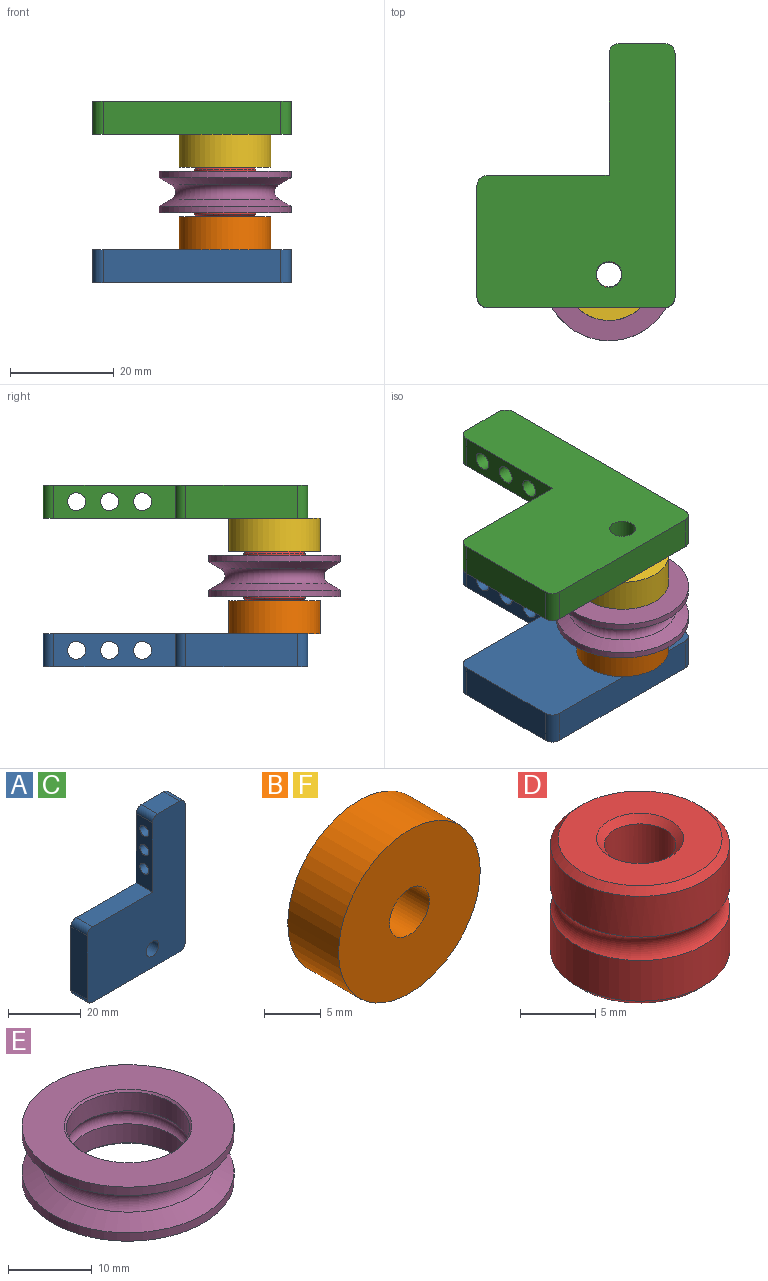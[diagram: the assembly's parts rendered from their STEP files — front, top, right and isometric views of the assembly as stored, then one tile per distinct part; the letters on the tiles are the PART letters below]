
ASSEMBLY  parts=6 mates=5
PART A: 17 faces, bbox 38.1x6.4x50.8 mm
  f0: plane 23.4x6.35mm, normal (0,0,1), area 148.6mm2, adj f6,f7,f8,f9
  f1: plane 21.4x6.35mm, normal (-1,0,0), area 135.9mm2, adj f7,f8,f9,f10
  f2: plane 34.1x6.35mm, normal (0,0,-1), area 216.5mm2, adj f7,f8,f10,f11
  f3: plane 46.8x6.35mm, normal (1,0,0), area 269.1mm2, adj f7,f8,f11,f12,f14,f15,f16
  f4: plane 8.7x6.35mm, normal (0,0,1), area 55.2mm2, adj f7,f8,f12,f13
  f5: cylinder r=2.49mm len=6.35mm, axis (0,1,0), area 99.3mm2, adj f7,f8
  f6: plane 23.4x6.35mm, normal (-1,0,0), area 120.5mm2, adj f0,f7,f8,f13,f14,f15,f16
  f7: plane 50.8x38.1mm, normal (0,-1,0), area 1266.6mm2, adj f0,f1,f2,f3,f4,f5,f6,f9
  f8: plane 50.8x38.1mm, normal (0,1,0), area 1266.6mm2, adj f0,f1,f2,f3,f4,f5,f6,f9
  f9: cylinder r=2mm len=6.35mm, axis (0,-1,0), area 19.9mm2, adj f0,f1,f7,f8
  f10: cylinder r=2mm len=6.35mm, axis (0,1,0), area 19.9mm2, adj f1,f2,f7,f8
  f11: cylinder r=2mm len=6.35mm, axis (0,-1,0), area 19.9mm2, adj f2,f3,f7,f8
  f12: cylinder r=2mm len=6.35mm, axis (0,1,0), area 19.9mm2, adj f3,f4,f7,f8
  f13: cylinder r=2mm len=6.35mm, axis (0,-1,0), area 19.9mm2, adj f4,f6,f7,f8
  f14: cylinder r=1.73mm len=12.7mm, axis (-1,0,0), area 137.8mm2, adj f3,f6
  f15: cylinder r=1.73mm len=12.7mm, axis (-1,0,0), area 137.8mm2, adj f3,f6
  f16: cylinder r=1.73mm len=12.7mm, axis (-1,0,0), area 137.8mm2, adj f3,f6
PART B: 4 faces, bbox 17.7x6.4x17.7 mm
  f0: cylinder r=2.49mm len=6.35mm, axis (0,1,0), area 99.3mm2, adj f2,f3
  f1: cylinder r=8.84mm len=17.68mm, axis (0,1,0), area 352.7mm2, adj f2,f3
  f2: plane 17.68x17.68mm, normal (0,-1,0), area 226mm2, adj f0,f1
  f3: plane 17.68x17.68mm, normal (0,1,0), area 226mm2, adj f0,f1
PART C: same geometry as A
PART D: 10 faces, bbox 14.4x14.4x9.5 mm
  f0: torus R=6.67mm, axis (0,0,1), area 78.3mm2, adj f5,f6
  f1: cone r=2.38mm half-angle=45deg, axis (0,0,1), area 11.9mm2, adj f7,f8
  f2: cone r=5.45mm half-angle=45deg, axis (0,0,-1), area 25.7mm2, adj f5,f8
  f3: cone r=5.95mm half-angle=45deg, axis (0,0,1), area 25.7mm2, adj f6,f9
  f4: cone r=2.89mm half-angle=45deg, axis (0,0,-1), area 11.9mm2, adj f7,f9
  f5: cylinder r=5.95mm len=11.91mm, axis (0,0,1), area 123.5mm2, adj f0,f2
  f6: cylinder r=5.95mm len=11.91mm, axis (0,0,1), area 123.5mm2, adj f0,f3
  f7: cylinder r=2.38mm len=8.51mm, axis (0,0,1), area 127.3mm2, adj f1,f4
  f8: plane 10.89x10.89mm, normal (0,0,1), area 66.9mm2, adj f1,f2
  f9: plane 10.89x10.89mm, normal (0,0,-1), area 66.9mm2, adj f3,f4
PART E: 12 faces, bbox 25.4x25.4x7.9 mm
  f0: torus R=11.11mm, axis (0,0,1), area 206mm2, adj f3,f9
  f1: cone r=7.38mm half-angle=45deg, axis (0,0,1), area 16.9mm2, adj f7,f10
  f2: cone r=7.64mm half-angle=45deg, axis (0,0,-1), area 16.9mm2, adj f5,f11
  f3: cone r=12.7mm half-angle=60.3deg, axis (0,0,-1), area 197.5mm2, adj f0,f4
  f4: cylinder r=12.7mm len=25.4mm, axis (0,0,1), area 98.3mm2, adj f3,f11
  f5: cylinder r=7.38mm len=14.76mm, axis (0,0,1), area 127.8mm2, adj f2,f6
  f6: torus R=6.67mm, axis (0,0,1), area 106.8mm2, adj f5,f7
  f7: cylinder r=7.38mm len=14.76mm, axis (0,0,1), area 127.8mm2, adj f1,f6
  f8: cylinder r=12.7mm len=25.4mm, axis (0,0,1), area 98.3mm2, adj f9,f10
  f9: cone r=10.33mm half-angle=60.3deg, axis (0,0,1), area 197.5mm2, adj f0,f8
  f10: plane 25.4x25.4mm, normal (0,0,1), area 323.5mm2, adj f1,f8
  f11: plane 25.4x25.4mm, normal (0,0,-1), area 323.5mm2, adj f2,f4
PART F: same geometry as B
PLACE A rot(axis=(-1,0,0),90deg) t=(-9.17,18.2,-13.13)mm
PLACE B rot(axis=(1,0,0),90deg) t=(-2.82,-0.85,-6.78)mm
PLACE C rot(axis=(-1,0,0),90deg) t=(-9.17,18.2,15.45)mm
PLACE D t=(-2.82,-0.85,1.16)mm
PLACE E t=(-2.82,-0.85,1.16)mm
PLACE F rot(axis=(-0.58,0.58,-0.58),120deg) t=(-2.82,-0.85,9.1)mm
MATE fastened B.f0 <-> A.f5  axis (0,0,-1) through (-2.82,-0.85,-9.95)mm
MATE fastened F.f1 <-> C.f5  axis (0,0,1) through (-2.82,-0.85,12.27)mm
MATE fastened E.f0 <-> D.f0  axis (0,0,1) through (-2.82,-0.85,1.16)mm
MATE fastened C.f5 <-> D.f0  axis (0,0,-1) through (-2.82,-0.85,12.27)mm
MATE fastened A.f5 <-> D.f0  axis (0,0,1) through (-2.82,-0.85,-9.95)mm
